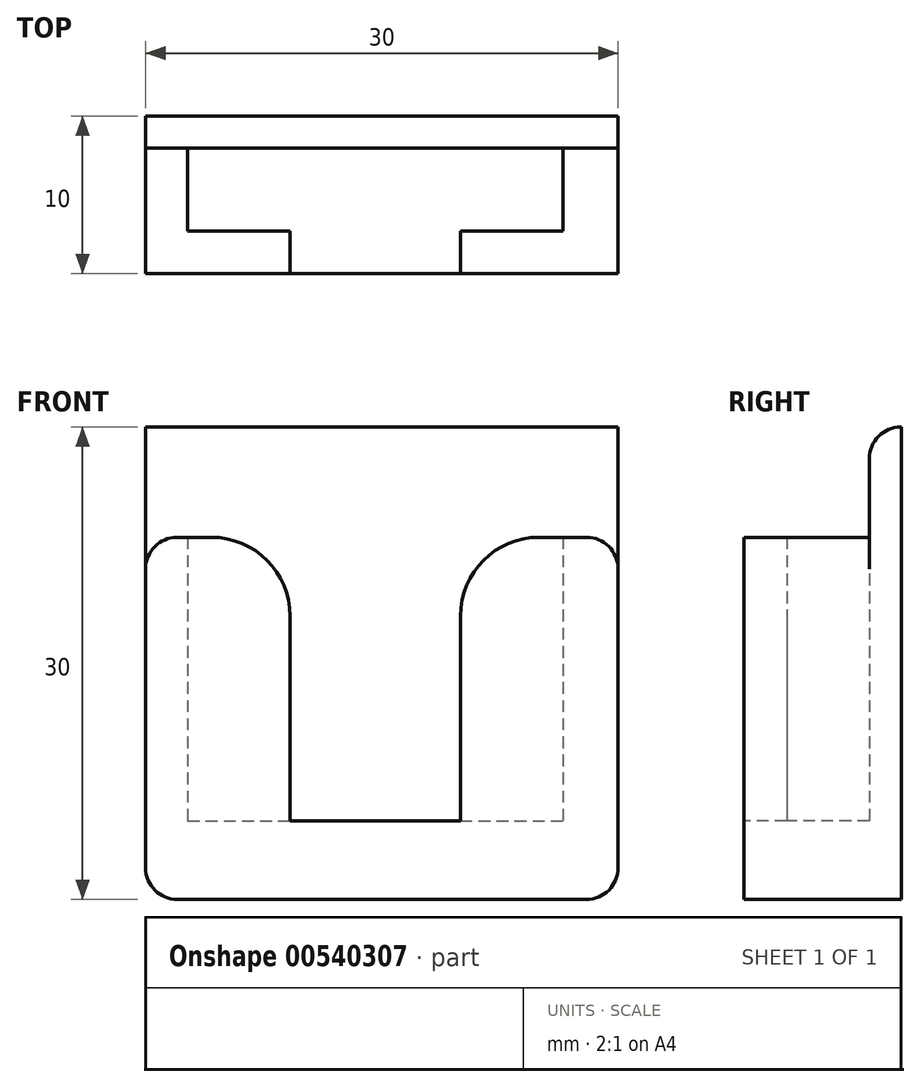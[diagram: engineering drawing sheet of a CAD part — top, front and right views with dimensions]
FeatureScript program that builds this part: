
annotation { "Feature Type Name" : "Feature", "Feature Type Description" : "" }
export const myFeature = defineFeature(function(context is Context, id is Id, definition is map)
    precondition{}
    {
        {
            var Q0;
            Q0=qCreatedBy(makeId("Top.planeOp"),FACE);
            var sketch = newSketch(context, id + "F0", { "sketchPlane" : qUnion([Q0])});
            skLineSegment(sketch, "E0.bottom", {"start": v(-14.38, 4.87) * mm, "end": v(15.62, 4.87) * mm});
            skLineSegment(sketch, "E0.top", {"start": v(-14.38, -5.13) * mm, "end": v(15.62, -5.13) * mm});
            skLineSegment(sketch, "E0.left", {"start": v(-14.38, 4.87) * mm, "end": v(-14.38, -5.13) * mm});
            skLineSegment(sketch, "E0.right", {"start": v(15.62, 4.87) * mm, "end": v(15.62, -5.13) * mm});
            skSolve(sketch);
        }
        {
            var Q0;
            Q0 = qSketchRegion(id + "F0", true);
            extrude(context, id + "F1", {"entities" : qUnion([Q0]), "depth" : 5 * mm, "offsetDistance" : 25 * mm});
        }
        {
            var Q0;
            Q0=makeQuery(id+"F1.opExtrude","CAP_FACE",FACE,{"disambiguationData":[OSD([sQuery(id+"F0.wireOp",EDGE,"E0.bottom"),sQuery(id+"F0.wireOp",EDGE,"E0.top"),sQuery(id+"F0.wireOp",EDGE,"E0.left"),sQuery(id+"F0.wireOp",EDGE,"E0.right")])],"isStart":false});
            var sketch = newSketch(context, id + "F2", { "sketchPlane" : qUnion([Q0])});
            skLineSegment(sketch, "E1.bottom", {"start": v(-14.38, 4.87) * mm, "end": v(15.62, 4.87) * mm});
            skLineSegment(sketch, "E1.top", {"start": v(-14.38, 2.83) * mm, "end": v(15.62, 2.83) * mm});
            skLineSegment(sketch, "E1.left", {"start": v(-14.38, 4.87) * mm, "end": v(-14.38, 2.83) * mm});
            skLineSegment(sketch, "E1.right", {"start": v(15.62, 4.87) * mm, "end": v(15.62, 2.83) * mm});
            skLineSegment(sketch, "E2", {"start": v(-11.71, 2.83) * mm, "end": v(-11.71, -2.41) * mm});
            skLineSegment(sketch, "E3", {"start": v(-11.71, -2.41) * mm, "end": v(-5.21, -2.41) * mm});
            skLineSegment(sketch, "E4", {"start": v(-5.21, -2.41) * mm, "end": v(-5.21, -5.13) * mm});
            skLineSegment(sketch, "E5", {"start": v(12.1, 2.83) * mm, "end": v(12.1, -2.41) * mm});
            skLineSegment(sketch, "E6", {"start": v(12.1, -2.41) * mm, "end": v(5.6, -2.41) * mm});
            skLineSegment(sketch, "E7", {"start": v(5.6, -2.41) * mm, "end": v(5.6, -5.13) * mm});
            skSolve(sketch);
        }
        {
            var Q0;
            Q0=makeQuery(id+"F2.imprint","IMPRINT",FACE,{"disambiguationData":[TD([[makeQuery(id+"F2.imprint","IMPRINT",EDGE,{"derivedFrom":sQuery(id+"F2.wireOp",EDGE,"E1.bottom")}),-1.0]])]});
            extrude(context, id + "F3", {"entities" : qUnion([Q0]), "operationType" : NewBodyOperationType.ADD, "depth" : 25 * mm, "offsetDistance" : 25 * mm});
        }
        {
            var Q0;
            {var subQ1=sQuery(id+"F2.wireOp",EDGE,"E2");Q0=makeQuery(id+"F2.imprint","IMPRINT",FACE,{"disambiguationData":[TD([[makeQuery(id+"F2.imprint","IMPRINT",EDGE,{"derivedFrom":subQ1}),-1.0]])]});}
            var Q1;
            {var subQ1=sQuery(id+"F2.wireOp",EDGE,"E5");Q1=makeQuery(id+"F2.imprint","IMPRINT",FACE,{"disambiguationData":[TD([[makeQuery(id+"F2.imprint","IMPRINT",EDGE,{"derivedFrom":subQ1}),1.0]])]});}
            extrude(context, id + "F4", {"entities" : qUnion([Q0, Q1]), "operationType" : NewBodyOperationType.ADD, "depth" : 18 * mm, "offsetDistance" : 25 * mm});
        }
        {
            var Q0;
            Q0=makeQuery(id+"F4.opExtrude","CAP_EDGE",EDGE,{"disambiguationData":[OSD([sQuery(id+"F2.wireOp",EDGE,"E4")])],"isStart":false});
            var Q1;
            Q1=makeQuery(id+"F4.opExtrude","CAP_EDGE",EDGE,{"disambiguationData":[OSD([sQuery(id+"F2.wireOp",EDGE,"E7")])],"isStart":false});
            fillet(context, id + "F5", {"entities" : qUnion([Q0, Q1]), "radius" : 5 * mm, "tangentPropagation" : true, "allowEdgeOverflow" : false});
        }
        {
            var Q0;
            Q0=makeQuery(id+"F3.opExtrude","CAP_EDGE",EDGE,{"disambiguationData":[OSD([sQuery(id+"F2.wireOp",EDGE,"E1.top")])],"isStart":false});
            var Q1;
            Q1=makeQuery(id+"F1.opExtrude","CAP_EDGE",EDGE,{"disambiguationData":[OSD([sQuery(id+"F0.wireOp",EDGE,"E0.right")])],"isStart":true});
            var Q2;
            Q2=makeQuery(id+"F4.opExtrude","CAP_EDGE",EDGE,{"disambiguationData":[OSD([sQuery(id+"F0.wireOp",EDGE,"E0.right")])],"isStart":false});
            var Q3;
            Q3=makeQuery(id+"F4.opExtrude","CAP_EDGE",EDGE,{"disambiguationData":[OSD([sQuery(id+"F0.wireOp",EDGE,"E0.left")])],"isStart":false});
            var Q4;
            Q4=makeQuery(id+"F1.opExtrude","CAP_EDGE",EDGE,{"disambiguationData":[OSD([sQuery(id+"F0.wireOp",EDGE,"E0.left")])],"isStart":true});
            fillet(context, id + "F6", {"entities" : qUnion([Q0, Q1, Q2, Q3, Q4]), "radius" : 2 * mm, "tangentPropagation" : true, "allowEdgeOverflow" : false});
        }
    });
